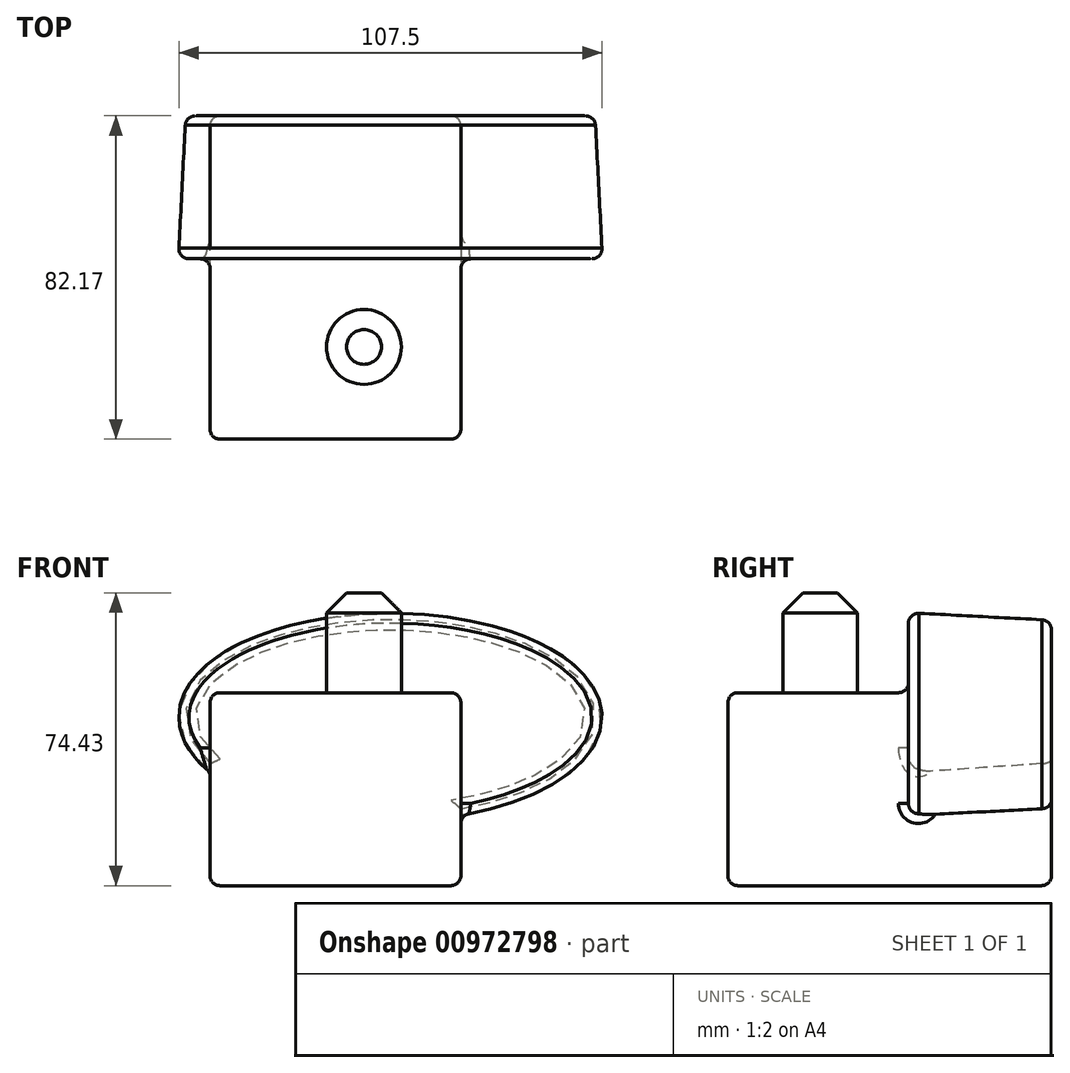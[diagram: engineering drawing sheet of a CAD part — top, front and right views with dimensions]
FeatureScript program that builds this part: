
annotation { "Feature Type Name" : "Feature", "Feature Type Description" : "" }
export const myFeature = defineFeature(function(context is Context, id is Id, definition is map)
    precondition{}
    {
        {
            var Q0;
            Q0=qCreatedBy(makeId("Front.planeOp"),FACE);
            var sketch = newSketch(context, id + "F0", { "sketchPlane" : qUnion([Q0])});
            skEllipse(sketch, "E0", {"center": v(19.88, 28.74) * mm, "majorRadius": 51.98 * mm, "minorRadius": 24.63 * mm, "majorAxis": v(-1, 0)});
            skSolve(sketch);
        }
        {
            var Q0;
            Q0 = qSketchRegion(id + "F0", true);
            extrude(context, id + "F1", {"entities" : qUnion([Q0]), "depth" : 36.32 * mm, "offsetDistance" : 25.4 * mm, "hasDraft" : true, "draftAngle" : 3 * degree});
        }
        {
            var Q0;
            Q0=qCreatedBy(makeId("Front.planeOp"),FACE);
            var sketch = newSketch(context, id + "F2", { "sketchPlane" : qUnion([Q0])});
            skLineSegment(sketch, "E1.bottom", {"start": v(-25.93, -14.08) * mm, "end": v(37.78, -14.08) * mm});
            skLineSegment(sketch, "E1.top", {"start": v(-25.93, 34.95) * mm, "end": v(37.78, 34.95) * mm});
            skLineSegment(sketch, "E1.left", {"start": v(-25.93, -14.08) * mm, "end": v(-25.93, 34.95) * mm});
            skLineSegment(sketch, "E1.right", {"start": v(37.78, -14.08) * mm, "end": v(37.78, 34.95) * mm});
            skSolve(sketch);
        }
        {
            var Q0;
            Q0 = qSketchRegion(id + "F2", true);
            extrude(context, id + "F3", {"entities" : qUnion([Q0]), "operationType" : NewBodyOperationType.ADD, "depth" : 82.17 * mm, "offsetDistance" : 25.4 * mm});
        }
        {
            var Q0;
            Q0=makeQuery(id+"F3.opExtrude","SWEPT_FACE",FACE,{"disambiguationData":[OSD([sQuery(id+"F2.wireOp",EDGE,"E1.top")])]});
            var Q1;
            Q1=makeQuery(id+"F3.boolean.opBoolean","INTERSECT",EDGE,{"derivedFrom":[makeQuery(id+"F1.opExtrude","CAP_FACE",FACE,{"disambiguationData":[OSD([sQuery(id+"F0.wireOp",EDGE,"E0")])],"isStart":false}),makeQuery(id+"F3.opExtrude","SWEPT_FACE",FACE,{"disambiguationData":[OSD([sQuery(id+"F2.wireOp",EDGE,"E1.top")])]})]});
            var Q2;
            Q2=makeQuery(id+"F1.opExtrude","CAP_FACE",FACE,{"disambiguationData":[OSD([sQuery(id+"F0.wireOp",EDGE,"E0")])],"isStart":false});
            var Q3;
            Q3=makeQuery(id+"F3.opExtrude","CAP_FACE",FACE,{"disambiguationData":[OSD([sQuery(id+"F2.wireOp",EDGE,"E1.bottom"),sQuery(id+"F2.wireOp",EDGE,"E1.top"),sQuery(id+"F2.wireOp",EDGE,"E1.left"),sQuery(id+"F2.wireOp",EDGE,"E1.right")])],"isStart":false});
            var Q4;
            Q4=makeQuery(id+"F3.opExtrude","SWEPT_FACE",FACE,{"disambiguationData":[OSD([sQuery(id+"F2.wireOp",EDGE,"E1.bottom")])]});
            var Q5;
            Q5=makeQuery(id+"F3.boolean.opBoolean","MERGE",FACE,{"derivedFrom":[makeQuery(id+"F1.opExtrude","CAP_FACE",FACE,{"disambiguationData":[OSD([sQuery(id+"F0.wireOp",EDGE,"E0")])],"isStart":true}),makeQuery(id+"F3.opExtrude","CAP_FACE",FACE,{"disambiguationData":[OSD([sQuery(id+"F2.wireOp",EDGE,"E1.bottom"),sQuery(id+"F2.wireOp",EDGE,"E1.top"),sQuery(id+"F2.wireOp",EDGE,"E1.left"),sQuery(id+"F2.wireOp",EDGE,"E1.right")])],"isStart":true})]});
            fillet(context, id + "F4", {"entities" : qUnion([Q0, Q1, Q2, Q3, Q4, Q5]), "radius" : 2.54 * mm, "tangentPropagation" : true, "allowEdgeOverflow" : false});
        }
        {
            var Q0;
            Q0=makeQuery(id+"F3.opExtrude","SWEPT_FACE",FACE,{"disambiguationData":[OSD([sQuery(id+"F2.wireOp",EDGE,"E1.top")])]});
            var sketch = newSketch(context, id + "F5", { "sketchPlane" : qUnion([Q0])});
            skCircle(sketch, "E2", {"center": v(13.17, -58.72) * mm, "radius": 9.5 * mm});
            skSolve(sketch);
        }
        {
            var Q0;
            Q0 = qSketchRegion(id + "F5", true);
            extrude(context, id + "F6", {"entities" : qUnion([Q0]), "operationType" : NewBodyOperationType.ADD, "depth" : 25.4 * mm, "offsetDistance" : 25.4 * mm});
        }
        {
            var Q0;
            Q0=makeQuery(id+"F6.opExtrude","CAP_EDGE",EDGE,{"disambiguationData":[OSD([sQuery(id+"F5.wireOp",EDGE,"E2")])],"isStart":false});
            chamfer(context, id + "F7", {"entities" : qUnion([Q0]), "width" : 5.08 * mm, "tangentPropagation" : true});
        }
    });
